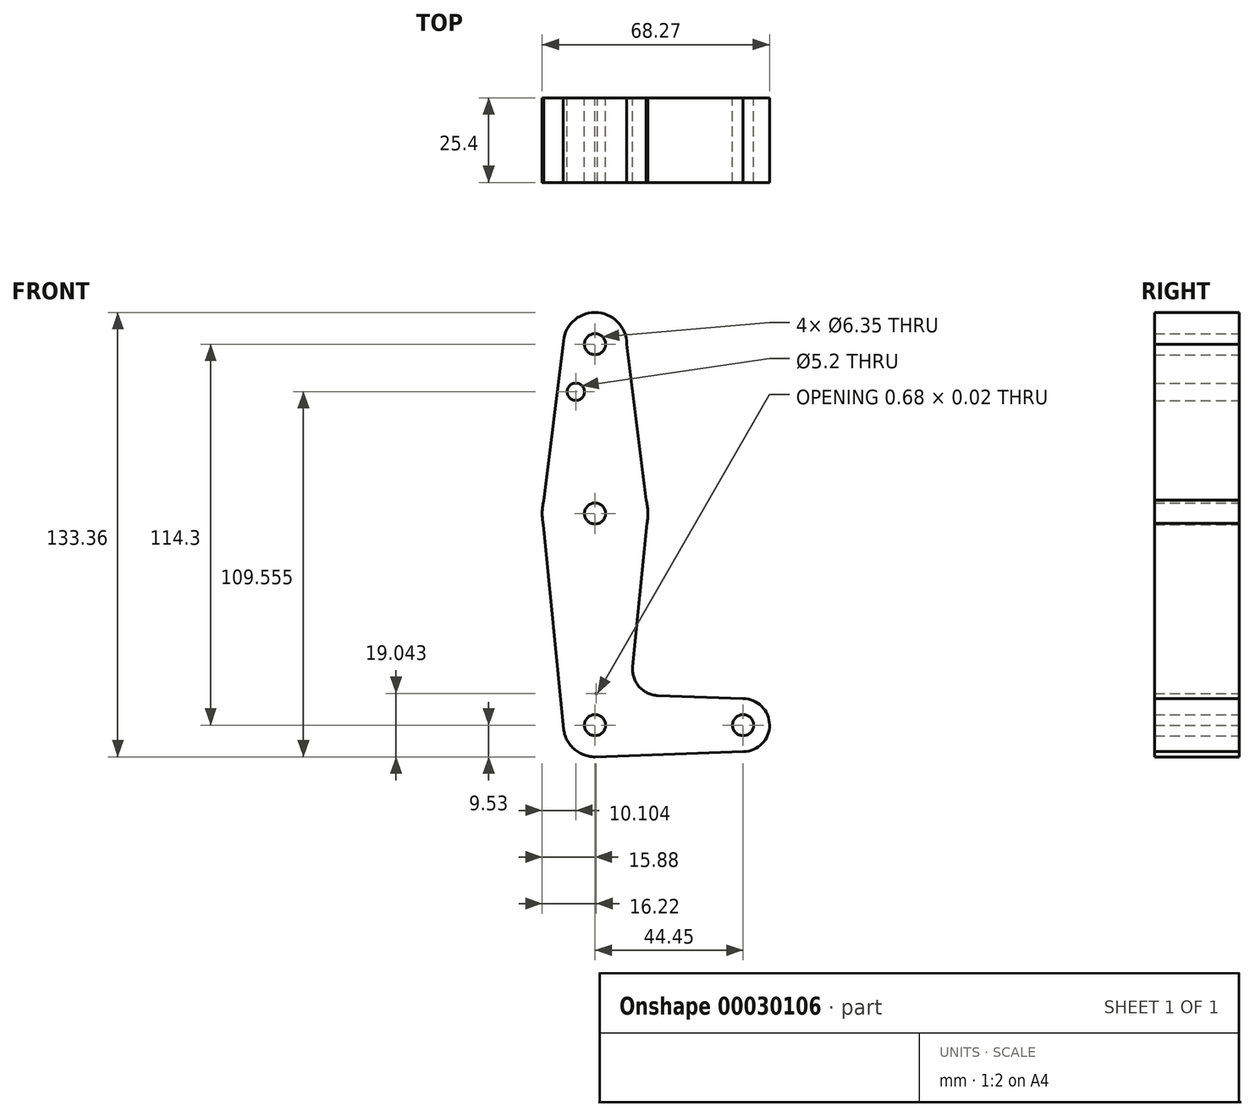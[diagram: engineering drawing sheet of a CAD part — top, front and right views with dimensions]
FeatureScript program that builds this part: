
annotation { "Feature Type Name" : "Feature", "Feature Type Description" : "" }
export const myFeature = defineFeature(function(context is Context, id is Id, definition is map)
    precondition{}
    {
        {
            var Q0;
            Q0=qCreatedBy(makeId("Front.planeOp"),FACE);
            var sketch = newSketch(context, id + "F0", { "sketchPlane" : qUnion([Q0])});
            skLineSegment(sketch, "E0", {"start": v(0, 0) * mm, "end": v(0, -50.8) * mm});
            skLineSegment(sketch, "E1", {"start": v(0, -50.8) * mm, "end": v(0, -114.3) * mm});
            skLineSegment(sketch, "E2", {"start": v(0, -114.3) * mm, "end": v(44.45, -114.3) * mm});
            skCircle(sketch, "E3", {"center": v(0, -50.8) * mm, "radius": 15.88 * mm});
            skCircle(sketch, "E4", {"center": v(0, -114.3) * mm, "radius": 9.53 * mm});
            skCircle(sketch, "E5", {"center": v(44.45, -114.3) * mm, "radius": 7.94 * mm});
            skCircle(sketch, "E6", {"center": v(0, 0) * mm, "radius": 9.53 * mm});
            skPoint(sketch, "E7", {"position": v(9.53, 0) * mm});
            skPoint(sketch, "E8", {"position": v(-9.53, 0) * mm});
            skPoint(sketch, "E9", {"position": v(-15.87, -50.6) * mm});
            skPoint(sketch, "E10", {"position": v(15.87, -50.95) * mm});
            skPoint(sketch, "E11", {"position": v(9.53, -114.3) * mm});
            skPoint(sketch, "E12", {"position": v(-9.52, -114.3) * mm});
            skPoint(sketch, "E13", {"position": v(36.51, -114.3) * mm});
            skPoint(sketch, "E14", {"position": v(44.6, -122.24) * mm});
            skPoint(sketch, "E15", {"position": v(44.45, -106.36) * mm});
            skPoint(sketch, "E16", {"position": v(0, -104.78) * mm});
            skLineSegment(sketch, "E17", {"start": v(0, -104.78) * mm, "end": v(0.68, -104.8) * mm});
            skLineSegment(sketch, "E18", {"start": v(0, -123.83) * mm, "end": v(44.6, -122.24) * mm});
            skLineSegment(sketch, "E19", {"start": v(11.29, -96.71) * mm, "end": v(15.87, -50.95) * mm});
            skLineSegment(sketch, "E20", {"start": v(-15.87, -50.6) * mm, "end": v(-9.52, -114.3) * mm});
            skLineSegment(sketch, "E21", {"start": v(9.53, 0) * mm, "end": v(15.87, -50.95) * mm});
            skLineSegment(sketch, "E22", {"start": v(-15.87, -50.6) * mm, "end": v(-9.53, 0) * mm});
            skLineSegment(sketch, "E23.trimOffspring", {"start": v(18.91, -105.45) * mm, "end": v(44.45, -106.36) * mm});
            skPoint(sketch, "E24.visualSharp", {"position": v(10.44, -105.15) * mm});
            skArc(sketch, "E24.filletArc", {"start": v(11.29, -96.71) * mm, "mid": v(13.2, -102.73) * mm, "end": v(18.91, -105.45) * mm});
            skCircle(sketch, "E25", {"center": v(0, 0) * mm, "radius": 3.17 * mm});
            skCircle(sketch, "E26", {"center": v(0, -50.8) * mm, "radius": 3.18 * mm});
            skCircle(sketch, "E27", {"center": v(0, -114.3) * mm, "radius": 3.17 * mm});
            skCircle(sketch, "E28", {"center": v(44.45, -114.3) * mm, "radius": 3.18 * mm});
            skCircle(sketch, "E29", {"center": v(-5.78, -14.27) * mm, "radius": 2.6 * mm});
            skSolve(sketch);
        }
        {
            var Q0;
            {var subQ0=sQuery(id+"F0.wireOp",EDGE,"E22");var subQ1=sQuery(id+"F0.wireOp",EDGE,"E3");var subQ2=makeQuery(id+"F0.imprint","INTERSECT",VERTEX,{"derivedFrom":[subQ1,subQ0]});Q0=makeQuery(id+"F0.imprint","IMPRINT",FACE,{"disambiguationData":[TD([[makeQuery(id+"F0.imprint","IMPRINT",EDGE,{"disambiguationData":[TD([[subQ2,-1.0]])],"derivedFrom":subQ1}),1.0]])]});}
            var Q1;
            {var subQ0=sQuery(id+"F0.wireOp",EDGE,"E20");var subQ1=sQuery(id+"F0.wireOp",EDGE,"E3");var subQ2=makeQuery(id+"F0.imprint","INTERSECT",VERTEX,{"derivedFrom":[subQ1,subQ0]});Q1=makeQuery(id+"F0.imprint","IMPRINT",FACE,{"disambiguationData":[TD([[makeQuery(id+"F0.imprint","IMPRINT",EDGE,{"disambiguationData":[TD([[subQ2,1.0]])],"derivedFrom":subQ1}),1.0]])]});}
            var Q2;
            {var subQ0=sQuery(id+"F0.wireOp",EDGE,"E19");var subQ1=sQuery(id+"F0.wireOp",EDGE,"E3");var subQ2=makeQuery(id+"F0.imprint","INTERSECT",VERTEX,{"derivedFrom":[subQ1,subQ0]});Q2=makeQuery(id+"F0.imprint","IMPRINT",FACE,{"disambiguationData":[TD([[makeQuery(id+"F0.imprint","IMPRINT",EDGE,{"disambiguationData":[TD([[subQ2,-1.0]])],"derivedFrom":subQ1}),1.0]])]});}
            var Q3;
            {var subQ0=sQuery(id+"F0.wireOp",EDGE,"E21");var subQ1=sQuery(id+"F0.wireOp",EDGE,"E3");var subQ2=makeQuery(id+"F0.imprint","INTERSECT",VERTEX,{"derivedFrom":[subQ1,subQ0]});Q3=makeQuery(id+"F0.imprint","IMPRINT",FACE,{"disambiguationData":[TD([[makeQuery(id+"F0.imprint","IMPRINT",EDGE,{"disambiguationData":[TD([[subQ2,1.0]])],"derivedFrom":subQ1}),1.0]])]});}
            var Q4;
            {var subQ0=sQuery(id+"F0.wireOp",EDGE,"E18");var subQ1=sQuery(id+"F0.wireOp",EDGE,"E4");var subQ3=makeQuery(id+"F0.imprint","INTERSECT",VERTEX,{"disambiguationData":[OD(0.0)],"derivedFrom":[subQ1,subQ0]});Q4=makeQuery(id+"F0.imprint","IMPRINT",FACE,{"disambiguationData":[TD([[makeQuery(id+"F0.imprint","IMPRINT",EDGE,{"disambiguationData":[TD([[subQ3,-1.0]])],"derivedFrom":subQ1}),1.0]])]});}
            var Q5;
            {var subQ3=sQuery(id+"F0.wireOp",EDGE,"E6");var subQ5=sQuery(id+"F0.wireOp",EDGE,"E0");var subQ6=makeQuery(id+"F0.imprint","INTERSECT",VERTEX,{"derivedFrom":[subQ5,subQ3]});Q5=makeQuery(id+"F0.imprint","IMPRINT",FACE,{"disambiguationData":[TD([[makeQuery(id+"F0.imprint","IMPRINT",EDGE,{"disambiguationData":[TD([[subQ6,-1.0]])],"derivedFrom":subQ5}),1.0]])]});}
            var Q6;
            {var subQ0=sQuery(id+"F0.wireOp",EDGE,"E20");var subQ1=sQuery(id+"F0.wireOp",EDGE,"E3");var subQ2=makeQuery(id+"F0.imprint","INTERSECT",VERTEX,{"derivedFrom":[subQ1,subQ0]});Q6=makeQuery(id+"F0.imprint","IMPRINT",FACE,{"disambiguationData":[TD([[makeQuery(id+"F0.imprint","IMPRINT",EDGE,{"disambiguationData":[TD([[subQ2,-1.0]])],"derivedFrom":subQ1}),-1.0]])]});}
            var Q7;
            {var subQ3=sQuery(id+"F0.wireOp",EDGE,"E5");var subQ5=sQuery(id+"F0.wireOp",EDGE,"E2");var subQ6=makeQuery(id+"F0.imprint","INTERSECT",VERTEX,{"derivedFrom":[subQ5,subQ3]});Q7=makeQuery(id+"F0.imprint","IMPRINT",FACE,{"disambiguationData":[TD([[makeQuery(id+"F0.imprint","IMPRINT",EDGE,{"disambiguationData":[TD([[subQ6,1.0]])],"derivedFrom":subQ5}),-1.0]])]});}
            var Q8;
            Q8=makeQuery(id+"F0.imprint","IMPRINT",FACE,{"disambiguationData":[TD([[makeQuery(id+"F0.imprint","IMPRINT",EDGE,{"derivedFrom":sQuery(id+"F0.wireOp",EDGE,"E28")}),-1.0]])]});
            var Q9;
            Q9=makeQuery(id+"F0.imprint","IMPRINT",FACE,{"disambiguationData":[TD([[makeQuery(id+"F0.imprint","IMPRINT",EDGE,{"derivedFrom":sQuery(id+"F0.wireOp",EDGE,"E25")}),-1.0]])]});
            var Q10;
            {var subQ0=sQuery(id+"F0.wireOp",EDGE,"E27");var subQ1=sQuery(id+"F0.wireOp",EDGE,"E2");var subQ2=makeQuery(id+"F0.imprint","INTERSECT",VERTEX,{"derivedFrom":[subQ1,subQ0]});Q10=makeQuery(id+"F0.imprint","IMPRINT",FACE,{"disambiguationData":[TD([[makeQuery(id+"F0.imprint","IMPRINT",EDGE,{"disambiguationData":[TD([[subQ2,-1.0]])],"derivedFrom":subQ1}),-1.0]])]});}
            var Q11;
            {var subQ1=sQuery(id+"F0.wireOp",EDGE,"E23.trimOffspring");Q11=makeQuery(id+"F0.imprint","IMPRINT",FACE,{"disambiguationData":[TD([[makeQuery(id+"F0.imprint","IMPRINT",EDGE,{"derivedFrom":subQ1}),-1.0]])]});}
            var Q12;
            Q12=makeQuery(id+"F0.imprint","IMPRINT",FACE,{"disambiguationData":[TD([[makeQuery(id+"F0.imprint","IMPRINT",EDGE,{"derivedFrom":sQuery(id+"F0.wireOp",EDGE,"E29")}),-1.0]])]});
            var Q13;
            {var subQ3=sQuery(id+"F0.wireOp",EDGE,"E0");var subQ6=sQuery(id+"F0.wireOp",EDGE,"E3");var subQ11=makeQuery(id+"F0.imprint","INTERSECT",VERTEX,{"derivedFrom":[subQ3,subQ6]});Q13=makeQuery(id+"F0.imprint","IMPRINT",FACE,{"disambiguationData":[TD([[makeQuery(id+"F0.imprint","IMPRINT",EDGE,{"disambiguationData":[TD([[subQ11,-1.0]])],"derivedFrom":subQ3}),-1.0]])]});}
            var Q14;
            {var subQ3=sQuery(id+"F0.wireOp",EDGE,"E0");var subQ6=sQuery(id+"F0.wireOp",EDGE,"E3");var subQ12=makeQuery(id+"F0.imprint","INTERSECT",VERTEX,{"derivedFrom":[subQ3,subQ6]});Q14=makeQuery(id+"F0.imprint","IMPRINT",FACE,{"disambiguationData":[TD([[makeQuery(id+"F0.imprint","IMPRINT",EDGE,{"disambiguationData":[TD([[subQ12,-1.0]])],"derivedFrom":subQ3}),1.0]])]});}
            var Q15;
            {var subQ0=sQuery(id+"F0.wireOp",EDGE,"E17");Q15=makeQuery(id+"F0.imprint","IMPRINT",FACE,{"disambiguationData":[TD([[makeQuery(id+"F0.imprint","IMPRINT",EDGE,{"derivedFrom":subQ0}),-1.0]])]});}
            extrude(context, id + "F1", {"entities" : qUnion([Q0, Q1, Q2, Q3, Q4, Q5, Q6, Q7, Q8, Q9, Q10, Q11, Q12, Q13, Q14, Q15]), "depth" : 25.4 * mm});
        }
    });
